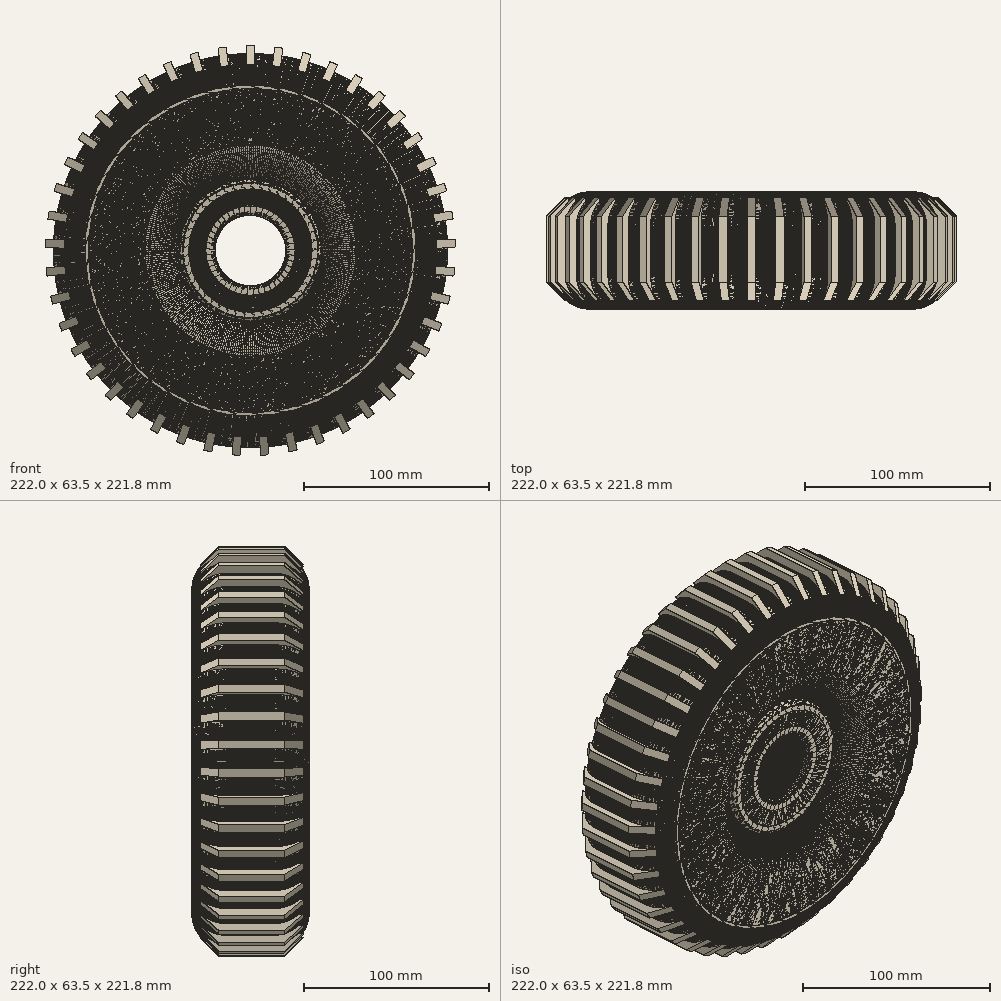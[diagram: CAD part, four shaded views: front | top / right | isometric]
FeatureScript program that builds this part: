
annotation { "Feature Type Name" : "Feature", "Feature Type Description" : "" }
export const myFeature = defineFeature(function(context is Context, id is Id, definition is map)
    precondition{}
    {
        {
            var Q0;
            Q0=qCreatedBy(makeId("Top.planeOp"),FACE);
            var sketch = newSketch(context, id + "F0", { "sketchPlane" : qUnion([Q0])});
            skLineSegment(sketch, "E0.bottom", {"start": v(38.1, -32.46) * mm, "end": v(106.68, -32.46) * mm});
            skLineSegment(sketch, "E0.top", {"start": v(38.1, 31.04) * mm, "end": v(106.68, 31.04) * mm});
            skLineSegment(sketch, "E0.left", {"start": v(38.1, -32.46) * mm, "end": v(38.1, 31.04) * mm});
            skLineSegment(sketch, "E0.right", {"start": v(106.68, -32.46) * mm, "end": v(106.68, 31.04) * mm});
            skPoint(sketch, "E0.middle", {"position": v(72.4, -0.7) * mm});
            skLineSegment(sketch, "E1.right", {"start": v(0, -31.52) * mm, "end": v(0, 32.46) * mm});
            skSolve(sketch);
        }
        {
            var Q0;
            {var subQ0=sQuery(id+"F0.wireOp",EDGE,"E0.bottom");Q0=makeQuery(id+"F0.imprint","IMPRINT",FACE,{"disambiguationData":[TD([[makeQuery(id+"F0.imprint","IMPRINT",EDGE,{"derivedFrom":subQ0}),1.0]])]});}
            var Q1;
            Q1=sQuery(id+"F0.wireOp",EDGE,"E1.right");
            revolve(context, id + "F1", {"entities" : qUnion([Q0]), "axis" : qUnion([Q1]), "revolveType" : RevolveType.FULL});
        }
        {
            var Q0;
            Q0=makeQuery(id+"F1.opRevolve","SWEPT_EDGE",EDGE,{"disambiguationData":[OSD([sQuery(id+"F0.wireOp",EDGE,"E0.bottom"),sQuery(id+"F0.wireOp",EDGE,"E0.right")])]});
            var Q1;
            Q1=makeQuery(id+"F1.opRevolve","SWEPT_EDGE",EDGE,{"disambiguationData":[OSD([sQuery(id+"F0.wireOp",EDGE,"E0.bottom"),sQuery(id+"F0.wireOp",EDGE,"E1.left")])]});
            var Q2;
            Q2=makeQuery(id+"F1.opRevolve","SWEPT_EDGE",EDGE,{"disambiguationData":[OSD([sQuery(id+"F0.wireOp",EDGE,"E0.top"),sQuery(id+"F0.wireOp",EDGE,"E0.right")])]});
            var Q3;
            Q3=makeQuery(id+"F1.opRevolve","SWEPT_EDGE",EDGE,{"disambiguationData":[OSD([sQuery(id+"F0.wireOp",EDGE,"E0.top"),sQuery(id+"F0.wireOp",EDGE,"E1.left")])]});
            fillet(context, id + "F2", {"entities" : qUnion([Q0, Q1, Q2, Q3]), "radius" : 19.05 * mm, "tangentPropagation" : true, "allowEdgeOverflow" : false});
        }
        {
            var Q0;
            Q0=qCreatedBy(makeId("Front.planeOp"),FACE);
            var sketch = newSketch(context, id + "F3", { "sketchPlane" : qUnion([Q0])});
            skCircle(sketch, "E2", {"center": v(0, 0) * mm, "radius": 38.36 * mm});
            skCircle(sketch, "E3", {"center": v(0, 0) * mm, "radius": 19.05 * mm});
            skSolve(sketch);
        }
        {
            var Q0;
            Q0=makeQuery(id+"F3.imprint","IMPRINT",FACE,{"disambiguationData":[TD([[makeQuery(id+"F3.imprint","IMPRINT",EDGE,{"derivedFrom":sQuery(id+"F3.wireOp",EDGE,"E2")}),1.0]])]});
            extrude(context, id + "F4", {"entities" : qUnion([Q0]), "operationType" : NewBodyOperationType.ADD, "endBound" : BoundingType.SYMMETRIC, "depth" : 50.8 * mm});
        }
        {
            var Q0;
            Q0=makeQuery(id+"F4.opExtrude","CAP_EDGE",EDGE,{"disambiguationData":[OSD([sQuery(id+"F3.wireOp",EDGE,"E2")])],"isStart":false});
            var Q1;
            Q1=makeQuery(id+"F4.opExtrude","CAP_EDGE",EDGE,{"disambiguationData":[OSD([sQuery(id+"F3.wireOp",EDGE,"E2")])],"isStart":true});
            var Q2;
            Q2=makeQuery(id+"F4.opExtrude","CAP_EDGE",EDGE,{"disambiguationData":[OSD([sQuery(id+"F3.wireOp",EDGE,"E3")])],"isStart":false});
            var Q3;
            Q3=makeQuery(id+"F4.opExtrude","CAP_EDGE",EDGE,{"disambiguationData":[OSD([sQuery(id+"F3.wireOp",EDGE,"E3")])],"isStart":true});
            fillet(context, id + "F5", {"entities" : qUnion([Q0, Q1, Q2, Q3]), "radius" : 5.08 * mm, "tangentPropagation" : true, "rho" : .75, "crossSection" : FilletCrossSection.CONIC, "allowEdgeOverflow" : false});
        }
        {
            var Q0;
            Q0=qCreatedBy(makeId("Front.planeOp"),FACE);
            var sketch = newSketch(context, id + "F6", { "sketchPlane" : qUnion([Q0])});
            skLineSegment(sketch, "E4.bottom", {"start": v(2.22, 110.97) * mm, "end": v(-2.22, 110.97) * mm});
            skLineSegment(sketch, "E4.top", {"start": v(2.22, 100.81) * mm, "end": v(-2.22, 100.81) * mm});
            skLineSegment(sketch, "E4.left", {"start": v(2.22, 110.97) * mm, "end": v(2.22, 100.81) * mm});
            skLineSegment(sketch, "E4.right", {"start": v(-2.22, 110.97) * mm, "end": v(-2.22, 100.81) * mm});
            skPoint(sketch, "E4.middle", {"position": v(0, 105.9) * mm});
            skCircle(sketch, "E5", {"center": v(0, 0) * mm, "radius": 12.7 * mm});
            skSolve(sketch);
        }
        {
            var Q0;
            Q0=makeQuery(id+"F6.imprint","IMPRINT",FACE,{"disambiguationData":[TD([[makeQuery(id+"F6.imprint","IMPRINT",EDGE,{"derivedFrom":sQuery(id+"F6.wireOp",EDGE,"E4.bottom")}),1.0]])]});
            extrude(context, id + "F7", {"entities" : qUnion([Q0]), "operationType" : NewBodyOperationType.ADD, "endBound" : BoundingType.SYMMETRIC, "depth" : 60.96 * mm});
        }
        {
            var Q0;
            Q0=makeQuery(id+"F7.opExtrude","CAP_EDGE",EDGE,{"disambiguationData":[OSD([sQuery(id+"F6.wireOp",EDGE,"E4.bottom")])],"isStart":true});
            var Q1;
            Q1=makeQuery(id+"F7.opExtrude","CAP_EDGE",EDGE,{"disambiguationData":[OSD([sQuery(id+"F6.wireOp",EDGE,"E4.bottom")])],"isStart":false});
            chamfer(context, id + "F8", {"entities" : qUnion([Q0, Q1]), "width" : 12.7 * mm, "tangentPropagation" : true});
        }
        {
            var Q0;
            Q0=makeQuery(id+"F1.opRevolve","SWEPT_BODY",BODY,{"disambiguationData":[OSD([sQuery(id+"F0.wireOp",EDGE,"E0.bottom"),sQuery(id+"F0.wireOp",EDGE,"E0.top"),sQuery(id+"F0.wireOp",EDGE,"E0.left"),sQuery(id+"F0.wireOp",EDGE,"E0.right")])]});
            var Q1;
            {var subQ0=sQuery(id+"F0.wireOp",EDGE,"E0.bottom");Q1=makeQuery(id+"F2.opFillet","BLEND_EDGE",EDGE,{"blendedFrom":[makeQuery(id+"F1.opRevolve","SWEPT_EDGE",EDGE,{"disambiguationData":[OSD([subQ0,sQuery(id+"F0.wireOp",EDGE,"E0.left")])]}),makeQuery(id+"F1.opRevolve","SWEPT_FACE",FACE,{"disambiguationData":[OSD([subQ0])]})],"blendedInto":[makeQuery(id+"F1.opRevolve","SWEPT_FACE",FACE,{"disambiguationData":[OSD([subQ0])]})]});}
            circularPattern(context, id + "F9", {"entities" : qUnion([Q0]), "axis" : qUnion([Q1]), "angle" : 360 * degree, "instanceCount" : 45, "equalSpace" : true});
        }
    });
